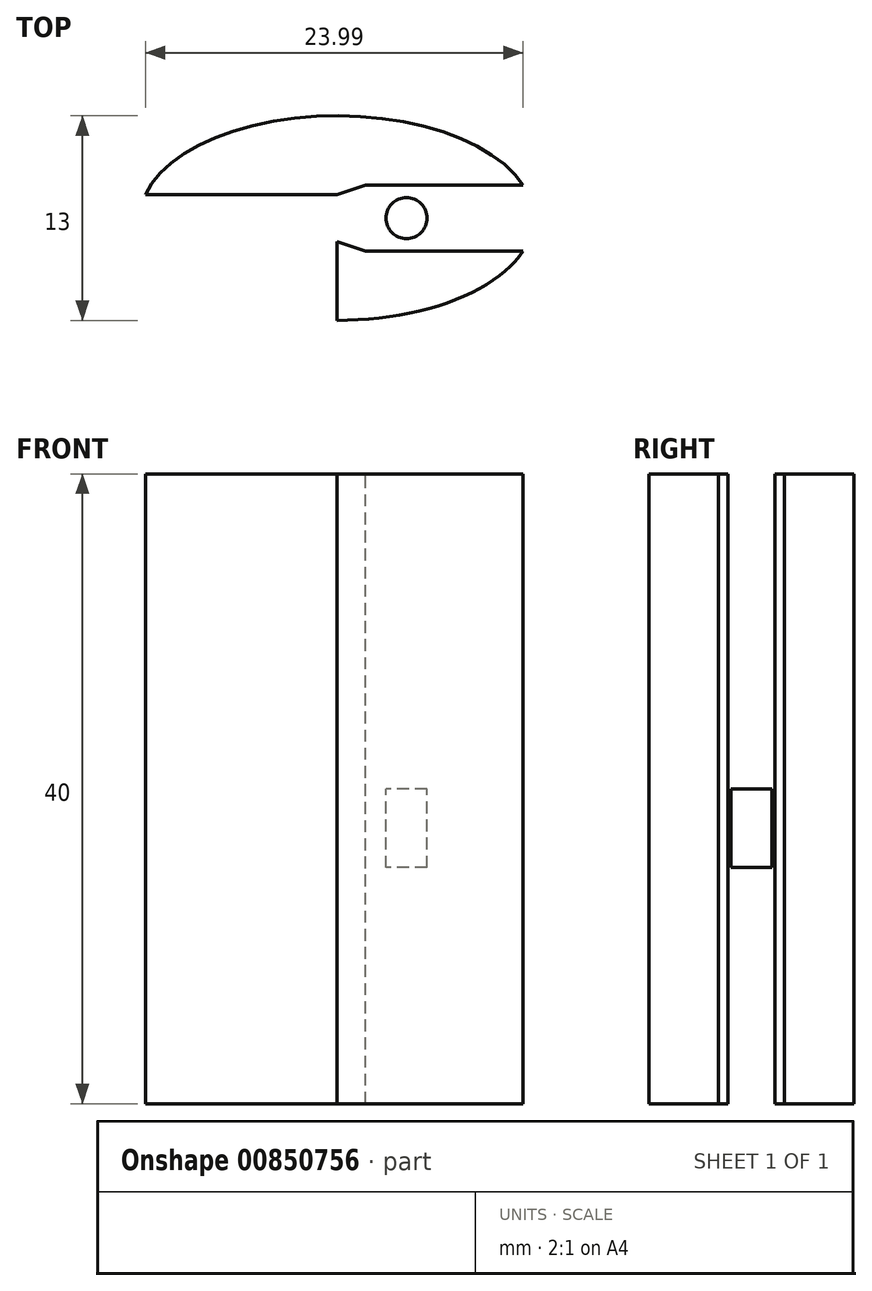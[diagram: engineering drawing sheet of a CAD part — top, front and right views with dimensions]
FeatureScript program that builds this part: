
annotation { "Feature Type Name" : "Feature", "Feature Type Description" : "" }
export const myFeature = defineFeature(function(context is Context, id is Id, definition is map)
    precondition{}
    {
        {
            var Q0;
            Q0=qCreatedBy(makeId("Top.planeOp"),FACE);
            var sketch = newSketch(context, id + "F0", { "sketchPlane" : qUnion([Q0])});
            skCircle(sketch, "E0", {"center": v(-7.17, -2.7) * mm, "radius": 1.2 * mm});
            skEllipse(sketch, "E1", {"center": v(0, 0) * mm, "majorRadius": 12.5 * mm, "minorRadius": 6.5 * mm, "majorAxis": v(-1, 0)});
            skLineSegment(sketch, "E2", {"start": v(0, -1.5) * mm, "end": v(-12.16, -1.5) * mm});
            skLineSegment(sketch, "E3", {"start": v(0, -1.5) * mm, "end": v(1.8, -2.1) * mm});
            skLineSegment(sketch, "E4.MirrorCS", {"start": v(0, 1.5) * mm, "end": v(-12.16, 1.5) * mm});
            skLineSegment(sketch, "E5.MirrorCS", {"start": v(0, 1.5) * mm, "end": v(1.8, 2.1) * mm});
            skLineSegment(sketch, "E6", {"start": v(1.8, -2.1) * mm, "end": v(11.83, -2.1) * mm});
            skLineSegment(sketch, "E7", {"start": v(1.8, 2.1) * mm, "end": v(11.83, 2.1) * mm});
            skCircle(sketch, "E8", {"center": v(-4.46, -2.54) * mm, "radius": 1.05 * mm});
            skLineSegment(sketch, "E9", {"start": v(0, -1.5) * mm, "end": v(0, -6.5) * mm});
            skLineSegment(sketch, "E10", {"start": v(-3.04, -4.35) * mm, "end": v(-3.04, -6.3) * mm});
            skLineSegment(sketch, "E11", {"start": v(-7.18, -3.9) * mm, "end": v(-4.53, -3.59) * mm});
            skLineSegment(sketch, "E12", {"start": v(-3.04, -4.35) * mm, "end": v(-3.04, -3.55) * mm});
            skLineSegment(sketch, "E13", {"start": v(-3.04, -3.55) * mm, "end": v(-4.16, -3.55) * mm});
            skLineSegment(sketch, "E14", {"start": v(-7.57, -1.5) * mm, "end": v(-7.57, -1.58) * mm});
            skCircle(sketch, "E15", {"center": v(4.42, 0) * mm, "radius": 1.3 * mm});
            skSolve(sketch);
        }
        {
            var Q0;
            {var subQ0=sQuery(id+"F0.wireOp",EDGE,"E10");Q0=makeQuery(id+"F0.imprint","IMPRINT",FACE,{"disambiguationData":[TD([[makeQuery(id+"F0.imprint","IMPRINT",EDGE,{"derivedFrom":subQ0}),-1.0]])]});}
            var Q1;
            {var subQ2=sQuery(id+"F0.wireOp",EDGE,"E3");Q1=makeQuery(id+"F0.imprint","IMPRINT",FACE,{"disambiguationData":[TD([[makeQuery(id+"F0.imprint","IMPRINT",EDGE,{"derivedFrom":subQ2}),1.0]])]});}
            var Q2;
            {var subQ0=sQuery(id+"F0.wireOp",EDGE,"E4.MirrorCS");Q2=makeQuery(id+"F0.imprint","IMPRINT",FACE,{"disambiguationData":[TD([[makeQuery(id+"F0.imprint","IMPRINT",EDGE,{"derivedFrom":subQ0}),-1.0]])]});}
            var Q3;
            Q3=makeQuery(id+"F0.imprint","IMPRINT",FACE,{"disambiguationData":[TD([[makeQuery(id+"F0.imprint","IMPRINT",EDGE,{"derivedFrom":sQuery(id+"F0.wireOp",EDGE,"E3")}),-1.0]])]});
            extrude(context, id + "F1", {"entities" : qUnion([Q0, Q1, Q2, Q3]), "oppositeDirection" : true, "depth" : 20 * mm, "offsetDistance" : 25 * mm});
        }
        {
            var Q0;
            {var subQ0=sQuery(id+"F0.wireOp",EDGE,"E10");Q0=makeQuery(id+"F0.imprint","IMPRINT",FACE,{"disambiguationData":[TD([[makeQuery(id+"F0.imprint","IMPRINT",EDGE,{"derivedFrom":subQ0}),-1.0]])]});}
            var Q1;
            {var subQ0=sQuery(id+"F0.wireOp",EDGE,"E4.MirrorCS");Q1=makeQuery(id+"F0.imprint","IMPRINT",FACE,{"disambiguationData":[TD([[makeQuery(id+"F0.imprint","IMPRINT",EDGE,{"derivedFrom":subQ0}),-1.0]])]});}
            var Q2;
            Q2=makeQuery(id+"F0.imprint","IMPRINT",FACE,{"disambiguationData":[TD([[makeQuery(id+"F0.imprint","IMPRINT",EDGE,{"derivedFrom":sQuery(id+"F0.wireOp",EDGE,"E3")}),-1.0]])]});
            extrude(context, id + "F2", {"entities" : qUnion([Q0, Q1, Q2]), "operationType" : NewBodyOperationType.ADD, "depth" : 20 * mm, "offsetDistance" : 25 * mm});
        }
        {
            var Q0;
            Q0=makeQuery(id+"F0.imprint","IMPRINT",FACE,{"disambiguationData":[TD([[makeQuery(id+"F0.imprint","IMPRINT",EDGE,{"derivedFrom":sQuery(id+"F0.wireOp",EDGE,"E15")}),1.0]])]});
            extrude(context, id + "F3", {"entities" : qUnion([Q0]), "operationType" : NewBodyOperationType.ADD, "oppositeDirection" : true, "depth" : 5 * mm, "offsetDistance" : 25 * mm});
        }
    });
